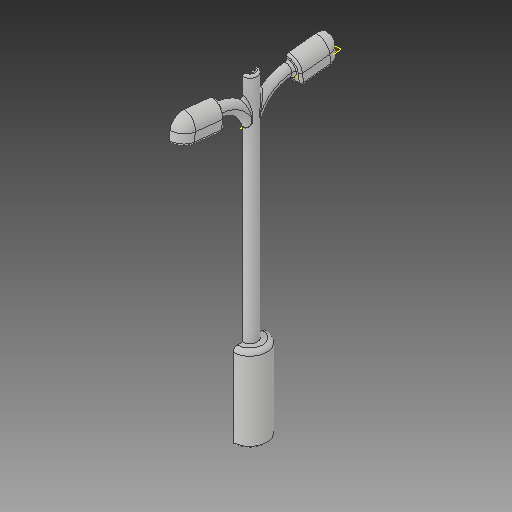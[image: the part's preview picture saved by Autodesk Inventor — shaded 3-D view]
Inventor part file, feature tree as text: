
AUTODESK INVENTOR PART (.ipt)
format: ipt  version: 2018 (Build 220112000, 112)  size: 513,536 bytes
history: native  units: in
note: dims shown in document units (in); Inventor stores cm internally (conversion verified against a paired STEP export)
features: sketch x11, other x3, plane x1
ambient origin geometry x8: Origin, YZ Plane, XZ Plane, XY Plane, X Axis, Y Axis, Z Axis, Center Point
bodies: Solid1 (feature_tree)
feature tree (15):
  other  "lampa_dual.ipt"
  other  "Solid1::lampa_dual.ipt"
  other  "TaggingFeature1"
  sketch  "Sketch1"  dims[d0=0.3937in]
  sketch  "Sketch6"
  sketch  "Sketch8"
  sketch  "Sketch9"
  sketch  "Sketch10"
  sketch  "Sketch11"
  sketch  "Sketch12"
  sketch  "Sketch13"
  sketch  "Sketch14"
  sketch  "Sketch15"
  sketch  "Sketch16"
  plane  "Work Plane1"
